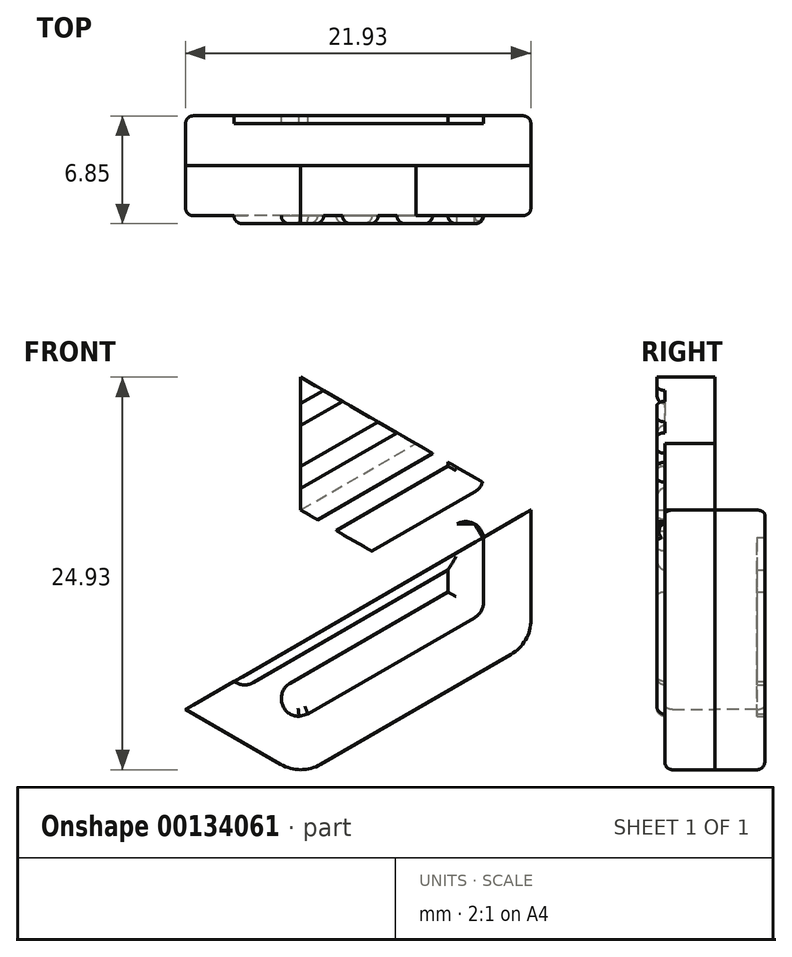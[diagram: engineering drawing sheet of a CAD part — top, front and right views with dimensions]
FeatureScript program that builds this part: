
annotation { "Feature Type Name" : "Feature", "Feature Type Description" : "" }
export const myFeature = defineFeature(function(context is Context, id is Id, definition is map)
    precondition{}
    {
        {
            var Q0;
            Q0=qCreatedBy(makeId("Front.planeOp"),FACE);
            var sketch = newSketch(context, id + "F0", { "sketchPlane" : qUnion([Q0])});
            skLineSegment(sketch, "E0", {"start": v(-0.1, -13.1) * mm, "end": v(-1.08, -12.54) * mm, "construction": true});
            skLineSegment(sketch, "E1", {"start": v(-1.08, -12.54) * mm, "end": v(-0.66, -11) * mm, "construction": true});
            skLineSegment(sketch, "E2", {"start": v(-0.66, -11) * mm, "end": v(9.36, -5.21) * mm});
            skLineSegment(sketch, "E3", {"start": v(9.36, -5.21) * mm, "end": v(9.36, -3.82) * mm});
            skLineSegment(sketch, "E4", {"start": v(9.36, -3.82) * mm, "end": v(-3, -10.95) * mm});
            skLineSegment(sketch, "E5", {"start": v(-3, -10.95) * mm, "end": v(-4.12, -10.95) * mm, "construction": true});
            skLineSegment(sketch, "E6", {"start": v(-4.12, -10.95) * mm, "end": v(-7.6, -8.96) * mm});
            skLineSegment(sketch, "E7", {"start": v(-7.6, -8.96) * mm, "end": v(-8.16, -7.98) * mm, "construction": true});
            skLineSegment(sketch, "E8", {"start": v(-8.16, -7.98) * mm, "end": v(-7.6, -7) * mm, "construction": true});
            skLineSegment(sketch, "E9", {"start": v(-7.6, -7) * mm, "end": v(9.36, 2.78) * mm});
            skLineSegment(sketch, "E10", {"start": v(9.36, 2.78) * mm, "end": v(9.36, 4.18) * mm});
            skLineSegment(sketch, "E11", {"start": v(9.36, 4.18) * mm, "end": v(-9.92, -6.96) * mm});
            skLineSegment(sketch, "E12", {"start": v(-9.92, -6.96) * mm, "end": v(-11.05, -6.96) * mm, "construction": true});
            skLineSegment(sketch, "E13", {"start": v(-11.05, -6.96) * mm, "end": v(-11.62, -5.98) * mm, "construction": true});
            skLineSegment(sketch, "E14", {"start": v(-11.62, -5.98) * mm, "end": v(-11.62, -1.98) * mm});
            skLineSegment(sketch, "E15", {"start": v(-11.62, -1.98) * mm, "end": v(-11.05, -1) * mm, "construction": true});
            skLineSegment(sketch, "E16", {"start": v(-11.05, -1) * mm, "end": v(4.78, 8.13) * mm});
            skLineSegment(sketch, "E17", {"start": v(4.78, 8.13) * mm, "end": v(3.57, 8.82) * mm});
            skLineSegment(sketch, "E18", {"start": v(3.57, 8.82) * mm, "end": v(-9.93, 1.04) * mm});
            skLineSegment(sketch, "E19", {"start": v(-9.93, 1.04) * mm, "end": v(-11.05, 1.04) * mm, "construction": true});
            skLineSegment(sketch, "E20", {"start": v(-11.05, 1.04) * mm, "end": v(-11.62, 2.02) * mm, "construction": true});
            skLineSegment(sketch, "E21", {"start": v(-11.62, 2.02) * mm, "end": v(-11.62, 6.01) * mm});
            skLineSegment(sketch, "E22", {"start": v(-11.62, 6.01) * mm, "end": v(-11.05, 7) * mm, "construction": true});
            skLineSegment(sketch, "E23", {"start": v(-11.05, 7) * mm, "end": v(-0.46, 13.1) * mm});
            skLineSegment(sketch, "E24", {"start": v(-0.46, 13.1) * mm, "end": v(1.08, 12.7) * mm, "construction": true});
            skLineSegment(sketch, "E25", {"start": v(1.08, 12.7) * mm, "end": v(0.67, 11.15) * mm, "construction": true});
            skLineSegment(sketch, "E26", {"start": v(0.67, 11.15) * mm, "end": v(-9.36, 5.36) * mm});
            skLineSegment(sketch, "E27", {"start": v(-9.36, 5.36) * mm, "end": v(-9.36, 3.97) * mm});
            skLineSegment(sketch, "E28", {"start": v(-9.36, 3.97) * mm, "end": v(3, 11.1) * mm});
            skLineSegment(sketch, "E29", {"start": v(3, 11.1) * mm, "end": v(4.14, 11.1) * mm, "construction": true});
            skLineSegment(sketch, "E30", {"start": v(4.14, 11.1) * mm, "end": v(7.6, 9.1) * mm});
            skLineSegment(sketch, "E31", {"start": v(7.6, 9.1) * mm, "end": v(8.16, 8.13) * mm, "construction": true});
            skLineSegment(sketch, "E32", {"start": v(8.16, 8.13) * mm, "end": v(7.6, 7.15) * mm, "construction": true});
            skLineSegment(sketch, "E33", {"start": v(7.6, 7.15) * mm, "end": v(-9.36, -2.63) * mm});
            skLineSegment(sketch, "E34", {"start": v(-9.36, -2.63) * mm, "end": v(-9.36, -4.03) * mm});
            skLineSegment(sketch, "E35", {"start": v(-9.36, -4.03) * mm, "end": v(9.93, 7.1) * mm});
            skLineSegment(sketch, "E36", {"start": v(9.93, 7.1) * mm, "end": v(11.05, 7.1) * mm, "construction": true});
            skLineSegment(sketch, "E37", {"start": v(11.05, 7.1) * mm, "end": v(11.62, 6.13) * mm, "construction": true});
            skLineSegment(sketch, "E38", {"start": v(11.62, 6.13) * mm, "end": v(11.62, 2.13) * mm});
            skLineSegment(sketch, "E39", {"start": v(11.62, 2.13) * mm, "end": v(11.05, 1.16) * mm, "construction": true});
            skLineSegment(sketch, "E40", {"start": v(11.05, 1.16) * mm, "end": v(-4.77, -7.98) * mm});
            skLineSegment(sketch, "E41", {"start": v(-4.77, -7.98) * mm, "end": v(-3.56, -8.67) * mm});
            skLineSegment(sketch, "E42", {"start": v(-3.56, -8.67) * mm, "end": v(9.93, -0.89) * mm});
            skLineSegment(sketch, "E43", {"start": v(9.93, -0.89) * mm, "end": v(11.05, -0.89) * mm, "construction": true});
            skLineSegment(sketch, "E44", {"start": v(11.05, -0.89) * mm, "end": v(11.62, -1.86) * mm, "construction": true});
            skLineSegment(sketch, "E45", {"start": v(11.62, -1.86) * mm, "end": v(11.62, -5.86) * mm});
            skLineSegment(sketch, "E46", {"start": v(11.62, -5.86) * mm, "end": v(11.05, -6.84) * mm, "construction": true});
            skLineSegment(sketch, "E47", {"start": v(11.05, -6.84) * mm, "end": v(0.46, -12.95) * mm});
            skLineSegment(sketch, "E48", {"start": v(0.46, -12.95) * mm, "end": v(-0.1, -13.1) * mm});
            skArc(sketch, "E49", {"start": v(0.67, 11.15) * mm, "mid": v(1.08, 12.7) * mm, "end": v(-0.46, 13.1) * mm});
            skArc(sketch, "E50", {"start": v(-11.05, 7) * mm, "mid": v(-11.47, 6.58) * mm, "end": v(-11.62, 6.01) * mm});
            skArc(sketch, "E51", {"start": v(-11.62, 2.02) * mm, "mid": v(-11.05, 1.04) * mm, "end": v(-9.93, 1.04) * mm});
            skArc(sketch, "E52", {"start": v(4.14, 11.1) * mm, "mid": v(3.57, 11.25) * mm, "end": v(3, 11.1) * mm});
            skArc(sketch, "E53", {"start": v(7.6, 7.15) * mm, "mid": v(8.16, 8.13) * mm, "end": v(7.6, 9.1) * mm});
            skArc(sketch, "E54", {"start": v(-11.05, -1) * mm, "mid": v(-11.47, -1.42) * mm, "end": v(-11.62, -1.98) * mm});
            skArc(sketch, "E55", {"start": v(-11.62, -5.98) * mm, "mid": v(-11.05, -6.96) * mm, "end": v(-9.92, -6.96) * mm});
            skArc(sketch, "E56", {"start": v(11.62, 6.13) * mm, "mid": v(11.05, 7.1) * mm, "end": v(9.93, 7.1) * mm});
            skArc(sketch, "E57", {"start": v(11.05, 1.16) * mm, "mid": v(11.47, 1.57) * mm, "end": v(11.62, 2.13) * mm});
            skArc(sketch, "E58", {"start": v(-7.6, -7) * mm, "mid": v(-8.16, -7.98) * mm, "end": v(-7.6, -8.96) * mm});
            skArc(sketch, "E59", {"start": v(-4.12, -10.95) * mm, "mid": v(-3.56, -11.1) * mm, "end": v(-3, -10.95) * mm});
            skArc(sketch, "E60", {"start": v(11.62, -1.86) * mm, "mid": v(11.05, -0.89) * mm, "end": v(9.93, -0.89) * mm});
            skArc(sketch, "E61", {"start": v(11.05, -6.84) * mm, "mid": v(11.47, -6.43) * mm, "end": v(11.62, -5.86) * mm});
            skArc(sketch, "E62", {"start": v(-0.66, -11) * mm, "mid": v(-1.2, -12.27) * mm, "end": v(-0.1, -13.1) * mm});
            skSolve(sketch);
        }
        {
            var Q0;
            Q0=qCreatedBy(makeId("Front.planeOp"),FACE);
            var sketch = newSketch(context, id + "F1", { "sketchPlane" : qUnion([Q0])});
            skLineSegment(sketch, "E63", {"start": v(1.27, -16.15) * mm, "end": v(13.35, -9.18) * mm});
            skLineSegment(sketch, "E64", {"start": v(14.62, -6.98) * mm, "end": v(14.62, 0) * mm});
            skLineSegment(sketch, "E65", {"start": v(14.62, 0) * mm, "end": v(0, 8.44) * mm});
            skLineSegment(sketch, "E66", {"start": v(0, 8.44) * mm, "end": v(0, 0) * mm});
            skLineSegment(sketch, "E67", {"start": v(0, 0) * mm, "end": v(-7.31, 4.22) * mm});
            skLineSegment(sketch, "E68", {"start": v(-7.31, 4.22) * mm, "end": v(-7.31, -12.66) * mm});
            skLineSegment(sketch, "E69", {"start": v(-1.27, -16.15) * mm, "end": v(-7.31, -12.66) * mm});
            skLineSegment(sketch, "E70", {"start": v(0, 0) * mm, "end": v(0, -8.44) * mm});
            skLineSegment(sketch, "E71", {"start": v(0, -8.44) * mm, "end": v(7.31, -4.22) * mm});
            skLineSegment(sketch, "E72", {"start": v(7.31, -4.22) * mm, "end": v(0, 0) * mm});
            skLineSegment(sketch, "E73", {"start": v(-7.31, -12.66) * mm, "end": v(14.62, 0) * mm});
            skLineSegment(sketch, "E74", {"start": v(0, 0) * mm, "end": v(3.66, -6.33) * mm, "construction": true});
            skLineSegment(sketch, "E75", {"start": v(7.31, -12.67) * mm, "end": v(3.66, -6.33) * mm, "construction": true});
            skPoint(sketch, "E76.visualSharp", {"position": v(0, -16.89) * mm});
            skArc(sketch, "E76.filletArc", {"start": v(-1.27, -16.15) * mm, "mid": v(0, -16.5) * mm, "end": v(1.27, -16.15) * mm});
            skPoint(sketch, "E77.visualSharp", {"position": v(14.62, -8.44) * mm});
            skArc(sketch, "E77.filletArc", {"start": v(13.35, -9.18) * mm, "mid": v(14.28, -8.25) * mm, "end": v(14.62, -6.98) * mm});
            skPoint(sketch, "E78.1.0", {"position": v(0, 16.89) * mm});
            skLineSegment(sketch, "E78.1.1", {"start": v(0, -8.44) * mm, "end": v(14.62, 0) * mm});
            skLineSegment(sketch, "E78.1.2", {"start": v(14.62, 0) * mm, "end": v(-7.31, 12.67) * mm});
            skLineSegment(sketch, "E78.1.3", {"start": v(13.35, 9.18) * mm, "end": v(1.27, 16.15) * mm});
            skLineSegment(sketch, "E78.1.5", {"start": v(-7.31, -4.22) * mm, "end": v(0, 0) * mm});
            skLineSegment(sketch, "E78.1.6", {"start": v(-7.31, 12.67) * mm, "end": v(-7.31, -4.22) * mm});
            skLineSegment(sketch, "E78.1.7", {"start": v(14.62, 6.98) * mm, "end": v(14.62, 0) * mm});
            skLineSegment(sketch, "E78.1.8", {"start": v(0, 0) * mm, "end": v(7.31, 4.22) * mm});
            skLineSegment(sketch, "E78.1.10", {"start": v(0, 0) * mm, "end": v(3.66, 6.33) * mm, "construction": true});
            skLineSegment(sketch, "E78.1.11", {"start": v(7.31, 12.66) * mm, "end": v(3.66, 6.33) * mm, "construction": true});
            skLineSegment(sketch, "E78.1.12", {"start": v(-1.27, 16.15) * mm, "end": v(-7.31, 12.67) * mm});
            skPoint(sketch, "E78.1.13", {"position": v(14.62, 8.44) * mm});
            skArc(sketch, "E78.1.14", {"start": v(14.62, 6.98) * mm, "mid": v(14.28, 8.25) * mm, "end": v(13.35, 9.18) * mm});
            skLineSegment(sketch, "E78.1.15", {"start": v(7.31, 4.22) * mm, "end": v(0, 8.44) * mm});
            skArc(sketch, "E78.1.16", {"start": v(1.27, 16.15) * mm, "mid": v(0, 16.5) * mm, "end": v(-1.27, 16.15) * mm});
            skPoint(sketch, "E78.2.0", {"position": v(-14.62, -8.44) * mm});
            skLineSegment(sketch, "E78.2.1", {"start": v(7.31, 4.22) * mm, "end": v(-7.31, 12.67) * mm});
            skLineSegment(sketch, "E78.2.2", {"start": v(-7.31, 12.67) * mm, "end": v(-7.31, -12.66) * mm});
            skLineSegment(sketch, "E78.2.3", {"start": v(-14.62, 6.98) * mm, "end": v(-14.62, -6.98) * mm});
            skLineSegment(sketch, "E78.2.4", {"start": v(0, 0) * mm, "end": v(7.31, 4.22) * mm});
            skLineSegment(sketch, "E78.2.6", {"start": v(-7.31, -12.66) * mm, "end": v(7.31, -4.22) * mm});
            skLineSegment(sketch, "E78.2.7", {"start": v(-13.35, 9.18) * mm, "end": v(-7.31, 12.67) * mm});
            skLineSegment(sketch, "E78.2.9", {"start": v(-7.31, -4.22) * mm, "end": v(0, 0) * mm});
            skLineSegment(sketch, "E78.2.10", {"start": v(0, 0) * mm, "end": v(-7.31, 0) * mm, "construction": true});
            skLineSegment(sketch, "E78.2.11", {"start": v(-14.62, 0) * mm, "end": v(-7.31, 0) * mm, "construction": true});
            skLineSegment(sketch, "E78.2.12", {"start": v(-13.35, -9.18) * mm, "end": v(-7.31, -12.66) * mm});
            skPoint(sketch, "E78.2.13", {"position": v(-14.62, 8.44) * mm});
            skArc(sketch, "E78.2.14", {"start": v(-13.35, 9.18) * mm, "mid": v(-14.28, 8.25) * mm, "end": v(-14.62, 6.98) * mm});
            skLineSegment(sketch, "E78.2.15", {"start": v(-7.31, 4.22) * mm, "end": v(-7.31, -4.22) * mm});
            skArc(sketch, "E78.2.16", {"start": v(-14.62, -6.98) * mm, "mid": v(-14.28, -8.25) * mm, "end": v(-13.35, -9.18) * mm});
            skPoint(sketch, "E78.center", {"position": v(0, 0) * mm});
            skSolve(sketch);
        }
        {
            var Q0;
            Q0=makeQuery(id+"F1.imprint","IMPRINT",FACE,{"disambiguationData":[TD([[makeQuery(id+"F1.imprint","IMPRINT",EDGE,{"derivedFrom":sQuery(id+"F1.wireOp",EDGE,"E63")}),1.0]])]});
            var Q1;
            {var subQ0=sQuery(id+"F1.wireOp",EDGE,"E65");Q1=makeQuery(id+"F1.imprint","IMPRINT",FACE,{"disambiguationData":[TD([[makeQuery(id+"F1.imprint","IMPRINT",EDGE,{"derivedFrom":subQ0}),1.0]])]});}
            var Q2;
            Q2=makeQuery(id+"F1.imprint","IMPRINT",FACE,{"disambiguationData":[TD([[makeQuery(id+"F1.imprint","IMPRINT",EDGE,{"derivedFrom":sQuery(id+"F1.wireOp",EDGE,"E78.1.1")}),1.0]])]});
            var Q3;
            {var subQ0=sQuery(id+"F1.wireOp",EDGE,"E66");Q3=makeQuery(id+"F1.imprint","IMPRINT",FACE,{"disambiguationData":[TD([[makeQuery(id+"F1.imprint","IMPRINT",EDGE,{"derivedFrom":subQ0}),1.0]])]});}
            extrude(context, id + "F2", {"entities" : qUnion([Q0, Q1, Q2, Q3]), "depth" : 3.17 * mm});
        }
        {
            var Q0;
            Q0=makeQuery(id+"F1.imprint","IMPRINT",FACE,{"disambiguationData":[TD([[makeQuery(id+"F1.imprint","IMPRINT",EDGE,{"derivedFrom":sQuery(id+"F1.wireOp",EDGE,"E63")}),1.0]])]});
            var Q1;
            Q1=makeQuery(id+"F1.imprint","IMPRINT",FACE,{"disambiguationData":[TD([[makeQuery(id+"F1.imprint","IMPRINT",EDGE,{"derivedFrom":sQuery(id+"F1.wireOp",EDGE,"E67")}),1.0]])]});
            var Q2;
            {var subQ0=sQuery(id+"F1.wireOp",EDGE,"E70");Q2=makeQuery(id+"F1.imprint","IMPRINT",FACE,{"disambiguationData":[TD([[makeQuery(id+"F1.imprint","IMPRINT",EDGE,{"derivedFrom":subQ0}),-1.0]])]});}
            extrude(context, id + "F3", {"entities" : qUnion([Q0, Q1, Q2]), "oppositeDirection" : true, "depth" : 3.17 * mm});
        }
        {
            var Q0;
            Q0=makeQuery(id+"F2.opExtrude","CAP_FACE",FACE,{"disambiguationData":[OSD([sQuery(id+"F1.wireOp",EDGE,"E63"),sQuery(id+"F1.wireOp",EDGE,"E64"),sQuery(id+"F1.wireOp",EDGE,"E69"),sQuery(id+"F1.wireOp",EDGE,"E76.filletArc"),sQuery(id+"F1.wireOp",EDGE,"E77.filletArc"),sQuery(id+"F1.wireOp",EDGE,"E78.1.2"),sQuery(id+"F1.wireOp",EDGE,"E66"),sQuery(id+"F1.wireOp",EDGE,"E78.2.1"),sQuery(id+"F1.wireOp",EDGE,"E72"),sQuery(id+"F1.wireOp",EDGE,"E78.2.6")])],"isStart":false});
            var sketch = newSketch(context, id + "F4", { "sketchPlane" : qUnion([Q0])});
            skLineSegment(sketch, "E79.0", {"start": v(-0.1, -13.1) * mm, "end": v(-1.08, -12.54) * mm});
            skLineSegment(sketch, "E79.1", {"start": v(-1.08, -12.54) * mm, "end": v(-0.66, -11) * mm});
            skLineSegment(sketch, "E79.2", {"start": v(-0.66, -11) * mm, "end": v(9.36, -5.21) * mm});
            skLineSegment(sketch, "E79.3", {"start": v(9.36, -5.21) * mm, "end": v(9.36, -3.82) * mm});
            skLineSegment(sketch, "E79.4", {"start": v(9.36, -3.82) * mm, "end": v(-3, -10.95) * mm});
            skLineSegment(sketch, "E79.5", {"start": v(-3, -10.95) * mm, "end": v(-4.12, -10.95) * mm});
            skLineSegment(sketch, "E79.6", {"start": v(-4.12, -10.95) * mm, "end": v(-7.6, -8.96) * mm});
            skLineSegment(sketch, "E79.7", {"start": v(-7.6, -8.96) * mm, "end": v(-8.16, -7.98) * mm});
            skLineSegment(sketch, "E79.8", {"start": v(-8.16, -7.98) * mm, "end": v(-7.6, -7) * mm});
            skLineSegment(sketch, "E79.9", {"start": v(-7.6, -7) * mm, "end": v(9.36, 2.78) * mm});
            skLineSegment(sketch, "E79.10", {"start": v(9.36, 2.78) * mm, "end": v(9.36, 4.18) * mm});
            skLineSegment(sketch, "E79.11", {"start": v(9.36, 4.18) * mm, "end": v(-9.92, -6.96) * mm});
            skLineSegment(sketch, "E79.12", {"start": v(-9.92, -6.96) * mm, "end": v(-11.05, -6.96) * mm});
            skLineSegment(sketch, "E79.13", {"start": v(-11.05, -6.96) * mm, "end": v(-11.62, -5.98) * mm});
            skLineSegment(sketch, "E79.14", {"start": v(-11.62, -5.98) * mm, "end": v(-11.62, -1.98) * mm});
            skLineSegment(sketch, "E79.15", {"start": v(-11.62, -1.98) * mm, "end": v(-11.05, -1) * mm});
            skLineSegment(sketch, "E79.16", {"start": v(-11.05, -1) * mm, "end": v(4.78, 8.13) * mm});
            skLineSegment(sketch, "E79.17", {"start": v(4.78, 8.13) * mm, "end": v(3.57, 8.82) * mm});
            skLineSegment(sketch, "E79.18", {"start": v(3.57, 8.82) * mm, "end": v(-9.93, 1.04) * mm});
            skLineSegment(sketch, "E79.19", {"start": v(-9.93, 1.04) * mm, "end": v(-11.05, 1.04) * mm});
            skLineSegment(sketch, "E79.20", {"start": v(-11.05, 1.04) * mm, "end": v(-11.62, 2.02) * mm});
            skLineSegment(sketch, "E79.21", {"start": v(-11.62, 2.02) * mm, "end": v(-11.62, 6.01) * mm});
            skLineSegment(sketch, "E79.22", {"start": v(-11.62, 6.01) * mm, "end": v(-11.05, 7) * mm});
            skLineSegment(sketch, "E79.23", {"start": v(-11.05, 7) * mm, "end": v(-0.46, 13.1) * mm});
            skLineSegment(sketch, "E79.24", {"start": v(-0.46, 13.1) * mm, "end": v(1.08, 12.7) * mm});
            skLineSegment(sketch, "E79.25", {"start": v(1.08, 12.7) * mm, "end": v(0.67, 11.15) * mm});
            skLineSegment(sketch, "E79.26", {"start": v(0.67, 11.15) * mm, "end": v(-9.36, 5.36) * mm});
            skLineSegment(sketch, "E79.27", {"start": v(-9.36, 5.36) * mm, "end": v(-9.36, 3.97) * mm});
            skLineSegment(sketch, "E79.28", {"start": v(-9.36, 3.97) * mm, "end": v(3, 11.1) * mm});
            skLineSegment(sketch, "E79.29", {"start": v(3, 11.1) * mm, "end": v(4.14, 11.1) * mm});
            skLineSegment(sketch, "E79.30", {"start": v(4.14, 11.1) * mm, "end": v(7.6, 9.1) * mm});
            skLineSegment(sketch, "E79.31", {"start": v(7.6, 9.1) * mm, "end": v(8.16, 8.13) * mm});
            skLineSegment(sketch, "E79.32", {"start": v(8.16, 8.13) * mm, "end": v(7.6, 7.15) * mm});
            skLineSegment(sketch, "E79.33", {"start": v(7.6, 7.15) * mm, "end": v(-9.36, -2.63) * mm});
            skLineSegment(sketch, "E79.34", {"start": v(-9.36, -2.63) * mm, "end": v(-9.36, -4.03) * mm});
            skLineSegment(sketch, "E79.35", {"start": v(-9.36, -4.03) * mm, "end": v(9.93, 7.1) * mm});
            skLineSegment(sketch, "E79.36", {"start": v(9.93, 7.1) * mm, "end": v(11.05, 7.1) * mm});
            skLineSegment(sketch, "E79.37", {"start": v(11.05, 7.1) * mm, "end": v(11.62, 6.13) * mm});
            skLineSegment(sketch, "E79.38", {"start": v(11.62, 6.13) * mm, "end": v(11.62, 2.13) * mm});
            skLineSegment(sketch, "E79.39", {"start": v(11.62, 2.13) * mm, "end": v(11.05, 1.16) * mm});
            skLineSegment(sketch, "E79.40", {"start": v(11.05, 1.16) * mm, "end": v(-4.77, -7.98) * mm});
            skLineSegment(sketch, "E79.41", {"start": v(-4.77, -7.98) * mm, "end": v(-3.56, -8.67) * mm});
            skLineSegment(sketch, "E79.42", {"start": v(-3.56, -8.67) * mm, "end": v(9.93, -0.89) * mm});
            skLineSegment(sketch, "E79.43", {"start": v(9.93, -0.89) * mm, "end": v(11.05, -0.89) * mm});
            skLineSegment(sketch, "E79.44", {"start": v(11.05, -0.89) * mm, "end": v(11.62, -1.86) * mm});
            skLineSegment(sketch, "E79.45", {"start": v(11.62, -1.86) * mm, "end": v(11.62, -5.86) * mm});
            skLineSegment(sketch, "E79.46", {"start": v(11.62, -5.86) * mm, "end": v(11.05, -6.84) * mm});
            skLineSegment(sketch, "E79.47", {"start": v(11.05, -6.84) * mm, "end": v(0.46, -12.95) * mm});
            skLineSegment(sketch, "E79.48", {"start": v(0.46, -12.95) * mm, "end": v(-0.1, -13.1) * mm});
            skArc(sketch, "E79.49", {"start": v(0.67, 11.15) * mm, "mid": v(1.08, 12.7) * mm, "end": v(-0.46, 13.1) * mm});
            skArc(sketch, "E79.50", {"start": v(-11.05, 7) * mm, "mid": v(-11.47, 6.58) * mm, "end": v(-11.62, 6.01) * mm});
            skArc(sketch, "E79.51", {"start": v(-11.62, 2.02) * mm, "mid": v(-11.05, 1.04) * mm, "end": v(-9.93, 1.04) * mm});
            skArc(sketch, "E79.52", {"start": v(4.14, 11.1) * mm, "mid": v(3.57, 11.25) * mm, "end": v(3, 11.1) * mm});
            skArc(sketch, "E79.53", {"start": v(7.6, 7.15) * mm, "mid": v(8.16, 8.13) * mm, "end": v(7.6, 9.1) * mm});
            skArc(sketch, "E79.54", {"start": v(-11.05, -1) * mm, "mid": v(-11.47, -1.42) * mm, "end": v(-11.62, -1.98) * mm});
            skArc(sketch, "E79.55", {"start": v(-11.62, -5.98) * mm, "mid": v(-11.05, -6.96) * mm, "end": v(-9.92, -6.96) * mm});
            skArc(sketch, "E79.56", {"start": v(11.62, 6.13) * mm, "mid": v(11.05, 7.1) * mm, "end": v(9.93, 7.1) * mm});
            skArc(sketch, "E79.57", {"start": v(11.05, 1.16) * mm, "mid": v(11.47, 1.57) * mm, "end": v(11.62, 2.13) * mm});
            skArc(sketch, "E79.58", {"start": v(-7.6, -7) * mm, "mid": v(-8.16, -7.98) * mm, "end": v(-7.6, -8.96) * mm});
            skArc(sketch, "E79.59", {"start": v(-4.12, -10.95) * mm, "mid": v(-3.56, -11.1) * mm, "end": v(-3, -10.95) * mm});
            skArc(sketch, "E79.60", {"start": v(11.62, -1.86) * mm, "mid": v(11.05, -0.89) * mm, "end": v(9.93, -0.89) * mm});
            skArc(sketch, "E79.61", {"start": v(11.05, -6.84) * mm, "mid": v(11.47, -6.43) * mm, "end": v(11.62, -5.86) * mm});
            skArc(sketch, "E79.62", {"start": v(-0.66, -11) * mm, "mid": v(-1.2, -12.27) * mm, "end": v(-0.1, -13.1) * mm});
            skLineSegment(sketch, "E80.0", {"start": v(-1.27, -16.15) * mm, "end": v(-7.31, -12.66) * mm});
            skArc(sketch, "E80.1", {"start": v(-1.27, -16.15) * mm, "mid": v(0, -16.5) * mm, "end": v(1.27, -16.15) * mm});
            skLineSegment(sketch, "E80.2", {"start": v(1.27, -16.15) * mm, "end": v(13.35, -9.18) * mm});
            skArc(sketch, "E80.3", {"start": v(13.35, -9.18) * mm, "mid": v(14.28, -8.25) * mm, "end": v(14.62, -6.98) * mm});
            skLineSegment(sketch, "E80.4", {"start": v(14.62, -6.98) * mm, "end": v(14.62, 0) * mm});
            skLineSegment(sketch, "E80.5", {"start": v(-7.31, -12.66) * mm, "end": v(7.31, -4.22) * mm});
            skLineSegment(sketch, "E80.6", {"start": v(14.62, 0) * mm, "end": v(0, 8.44) * mm});
            skLineSegment(sketch, "E80.7", {"start": v(7.31, -4.22) * mm, "end": v(0, 0) * mm});
            skLineSegment(sketch, "E80.8", {"start": v(0, 8.44) * mm, "end": v(0, 0) * mm});
            skSolve(sketch);
        }
        {
            var Q0;
            Q0=makeQuery(id+"F3.opExtrude","CAP_FACE",FACE,{"disambiguationData":[OSD([sQuery(id+"F1.wireOp",EDGE,"E63"),sQuery(id+"F1.wireOp",EDGE,"E64"),sQuery(id+"F1.wireOp",EDGE,"E69"),sQuery(id+"F1.wireOp",EDGE,"E76.filletArc"),sQuery(id+"F1.wireOp",EDGE,"E77.filletArc"),sQuery(id+"F1.wireOp",EDGE,"E78.1.1"),sQuery(id+"F1.wireOp",EDGE,"E70"),sQuery(id+"F1.wireOp",EDGE,"E78.2.2"),sQuery(id+"F1.wireOp",EDGE,"E78.2.6"),sQuery(id+"F1.wireOp",EDGE,"E67"),sQuery(id+"F1.wireOp",EDGE,"E78.2.15")])],"isStart":false});
            var sketch = newSketch(context, id + "F5", { "sketchPlane" : qUnion([Q0])});
            skLineSegment(sketch, "E81.0", {"start": v(0.1, -13.1) * mm, "end": v(1.08, -12.54) * mm});
            skLineSegment(sketch, "E81.1", {"start": v(1.08, -12.54) * mm, "end": v(0.66, -11) * mm});
            skLineSegment(sketch, "E81.2", {"start": v(0.66, -11) * mm, "end": v(-9.36, -5.21) * mm});
            skLineSegment(sketch, "E81.3", {"start": v(-9.36, -5.21) * mm, "end": v(-9.36, -3.82) * mm});
            skLineSegment(sketch, "E81.4", {"start": v(-9.36, -3.82) * mm, "end": v(3, -10.95) * mm});
            skLineSegment(sketch, "E81.5", {"start": v(3, -10.95) * mm, "end": v(4.12, -10.95) * mm});
            skLineSegment(sketch, "E81.6", {"start": v(4.12, -10.95) * mm, "end": v(7.6, -8.96) * mm});
            skLineSegment(sketch, "E81.7", {"start": v(7.6, -8.96) * mm, "end": v(8.16, -7.98) * mm});
            skLineSegment(sketch, "E81.8", {"start": v(8.16, -7.98) * mm, "end": v(7.6, -7) * mm});
            skLineSegment(sketch, "E81.9", {"start": v(7.6, -7) * mm, "end": v(-9.36, 2.78) * mm});
            skLineSegment(sketch, "E81.10", {"start": v(-9.36, 2.78) * mm, "end": v(-9.36, 4.18) * mm});
            skLineSegment(sketch, "E81.11", {"start": v(-9.36, 4.18) * mm, "end": v(9.92, -6.96) * mm});
            skLineSegment(sketch, "E81.12", {"start": v(9.92, -6.96) * mm, "end": v(11.05, -6.96) * mm});
            skLineSegment(sketch, "E81.13", {"start": v(11.05, -6.96) * mm, "end": v(11.62, -5.98) * mm});
            skLineSegment(sketch, "E81.14", {"start": v(11.62, -5.98) * mm, "end": v(11.62, -1.98) * mm});
            skLineSegment(sketch, "E81.15", {"start": v(11.62, -1.98) * mm, "end": v(11.05, -1) * mm});
            skLineSegment(sketch, "E81.16", {"start": v(11.05, -1) * mm, "end": v(-4.78, 8.13) * mm});
            skLineSegment(sketch, "E81.17", {"start": v(-4.78, 8.13) * mm, "end": v(-3.57, 8.82) * mm});
            skLineSegment(sketch, "E81.18", {"start": v(-3.57, 8.82) * mm, "end": v(9.93, 1.04) * mm});
            skLineSegment(sketch, "E81.19", {"start": v(9.93, 1.04) * mm, "end": v(11.05, 1.04) * mm});
            skLineSegment(sketch, "E81.20", {"start": v(11.05, 1.04) * mm, "end": v(11.62, 2.02) * mm});
            skLineSegment(sketch, "E81.21", {"start": v(11.62, 2.02) * mm, "end": v(11.62, 6.01) * mm});
            skLineSegment(sketch, "E81.22", {"start": v(11.62, 6.01) * mm, "end": v(11.05, 7) * mm});
            skLineSegment(sketch, "E81.23", {"start": v(11.05, 7) * mm, "end": v(0.46, 13.1) * mm});
            skLineSegment(sketch, "E81.24", {"start": v(0.46, 13.1) * mm, "end": v(-1.08, 12.7) * mm});
            skLineSegment(sketch, "E81.25", {"start": v(-1.08, 12.7) * mm, "end": v(-0.67, 11.15) * mm});
            skLineSegment(sketch, "E81.26", {"start": v(-0.67, 11.15) * mm, "end": v(9.36, 5.36) * mm});
            skLineSegment(sketch, "E81.27", {"start": v(9.36, 5.36) * mm, "end": v(9.36, 3.97) * mm});
            skLineSegment(sketch, "E81.28", {"start": v(9.36, 3.97) * mm, "end": v(-3, 11.1) * mm});
            skLineSegment(sketch, "E81.29", {"start": v(-3, 11.1) * mm, "end": v(-4.14, 11.1) * mm});
            skLineSegment(sketch, "E81.30", {"start": v(-4.14, 11.1) * mm, "end": v(-7.6, 9.1) * mm});
            skLineSegment(sketch, "E81.31", {"start": v(-7.6, 9.1) * mm, "end": v(-8.16, 8.13) * mm});
            skLineSegment(sketch, "E81.32", {"start": v(-8.16, 8.13) * mm, "end": v(-7.6, 7.15) * mm});
            skLineSegment(sketch, "E81.33", {"start": v(-7.6, 7.15) * mm, "end": v(9.36, -2.63) * mm});
            skLineSegment(sketch, "E81.34", {"start": v(9.36, -2.63) * mm, "end": v(9.36, -4.03) * mm});
            skLineSegment(sketch, "E81.35", {"start": v(9.36, -4.03) * mm, "end": v(-9.93, 7.1) * mm});
            skLineSegment(sketch, "E81.36", {"start": v(-9.93, 7.1) * mm, "end": v(-11.05, 7.1) * mm});
            skLineSegment(sketch, "E81.37", {"start": v(-11.05, 7.1) * mm, "end": v(-11.62, 6.13) * mm});
            skLineSegment(sketch, "E81.38", {"start": v(-11.62, 6.13) * mm, "end": v(-11.62, 2.13) * mm});
            skLineSegment(sketch, "E81.39", {"start": v(-11.62, 2.13) * mm, "end": v(-11.05, 1.16) * mm});
            skLineSegment(sketch, "E81.40", {"start": v(-11.05, 1.16) * mm, "end": v(4.77, -7.98) * mm});
            skLineSegment(sketch, "E81.41", {"start": v(4.77, -7.98) * mm, "end": v(3.56, -8.67) * mm});
            skLineSegment(sketch, "E81.42", {"start": v(3.56, -8.67) * mm, "end": v(-9.93, -0.89) * mm});
            skLineSegment(sketch, "E81.43", {"start": v(-9.93, -0.89) * mm, "end": v(-11.05, -0.89) * mm});
            skLineSegment(sketch, "E81.44", {"start": v(-11.05, -0.89) * mm, "end": v(-11.62, -1.86) * mm});
            skLineSegment(sketch, "E81.45", {"start": v(-11.62, -1.86) * mm, "end": v(-11.62, -5.86) * mm});
            skLineSegment(sketch, "E81.46", {"start": v(-11.62, -5.86) * mm, "end": v(-11.05, -6.84) * mm});
            skLineSegment(sketch, "E81.47", {"start": v(-11.05, -6.84) * mm, "end": v(-0.46, -12.95) * mm});
            skLineSegment(sketch, "E81.48", {"start": v(-0.46, -12.95) * mm, "end": v(0.1, -13.1) * mm});
            skArc(sketch, "E81.49", {"start": v(-0.67, 11.15) * mm, "mid": v(-1.08, 12.7) * mm, "end": v(0.46, 13.1) * mm});
            skArc(sketch, "E81.50", {"start": v(11.05, 7) * mm, "mid": v(11.47, 6.58) * mm, "end": v(11.62, 6.01) * mm});
            skArc(sketch, "E81.51", {"start": v(11.62, 2.02) * mm, "mid": v(11.05, 1.04) * mm, "end": v(9.93, 1.04) * mm});
            skArc(sketch, "E81.52", {"start": v(-4.14, 11.1) * mm, "mid": v(-3.57, 11.25) * mm, "end": v(-3, 11.1) * mm});
            skArc(sketch, "E81.53", {"start": v(-7.6, 7.15) * mm, "mid": v(-8.16, 8.13) * mm, "end": v(-7.6, 9.1) * mm});
            skArc(sketch, "E81.54", {"start": v(11.05, -1) * mm, "mid": v(11.47, -1.42) * mm, "end": v(11.62, -1.98) * mm});
            skArc(sketch, "E81.55", {"start": v(11.62, -5.98) * mm, "mid": v(11.05, -6.96) * mm, "end": v(9.92, -6.96) * mm});
            skArc(sketch, "E81.56", {"start": v(-11.62, 6.13) * mm, "mid": v(-11.05, 7.1) * mm, "end": v(-9.93, 7.1) * mm});
            skArc(sketch, "E81.57", {"start": v(-11.05, 1.16) * mm, "mid": v(-11.47, 1.57) * mm, "end": v(-11.62, 2.13) * mm});
            skArc(sketch, "E81.58", {"start": v(7.6, -7) * mm, "mid": v(8.16, -7.98) * mm, "end": v(7.6, -8.96) * mm});
            skArc(sketch, "E81.59", {"start": v(4.12, -10.95) * mm, "mid": v(3.56, -11.1) * mm, "end": v(3, -10.95) * mm});
            skArc(sketch, "E81.60", {"start": v(-11.62, -1.86) * mm, "mid": v(-11.05, -0.89) * mm, "end": v(-9.93, -0.89) * mm});
            skArc(sketch, "E81.61", {"start": v(-11.05, -6.84) * mm, "mid": v(-11.47, -6.43) * mm, "end": v(-11.62, -5.86) * mm});
            skArc(sketch, "E81.62", {"start": v(0.66, -11) * mm, "mid": v(1.2, -12.27) * mm, "end": v(0.1, -13.1) * mm});
            skSolve(sketch);
        }
        {
            var Q0;
            Q0 = qSketchRegion(id + "F5", true);
            extrude(context, id + "F6", {"entities" : qUnion([Q0]), "operationType" : NewBodyOperationType.REMOVE, "oppositeDirection" : true, "depth" : .5 * mm});
        }
        {
            var Q0;
            Q0=makeQuery(id+"F4.imprint","IMPRINT",FACE,{"disambiguationData":[TD([[makeQuery(id+"F4.imprint","IMPRINT",EDGE,{"derivedFrom":sQuery(id+"F4.wireOp",EDGE,"E79.46")}),1.0]])]});
            var Q1;
            {var subQ0=sQuery(id+"F4.wireOp",EDGE,"E79.44");Q1=makeQuery(id+"F4.imprint","IMPRINT",FACE,{"disambiguationData":[TD([[makeQuery(id+"F4.imprint","IMPRINT",EDGE,{"derivedFrom":subQ0}),1.0]])]});}
            var Q2;
            {var subQ0=sQuery(id+"F4.wireOp",EDGE,"E79.43");Q2=makeQuery(id+"F4.imprint","IMPRINT",FACE,{"disambiguationData":[TD([[makeQuery(id+"F4.imprint","IMPRINT",EDGE,{"derivedFrom":subQ0}),1.0]])]});}
            var Q3;
            Q3=makeQuery(id+"F4.imprint","IMPRINT",FACE,{"disambiguationData":[TD([[makeQuery(id+"F4.imprint","IMPRINT",EDGE,{"derivedFrom":sQuery(id+"F4.wireOp",EDGE,"E79.5")}),1.0]])]});
            var Q4;
            {var subQ0=sQuery(id+"F4.wireOp",EDGE,"E79.1");Q4=makeQuery(id+"F4.imprint","IMPRINT",FACE,{"disambiguationData":[TD([[makeQuery(id+"F4.imprint","IMPRINT",EDGE,{"derivedFrom":subQ0}),1.0]])]});}
            var Q5;
            {var subQ0=sQuery(id+"F4.wireOp",EDGE,"E79.0");Q5=makeQuery(id+"F4.imprint","IMPRINT",FACE,{"disambiguationData":[TD([[makeQuery(id+"F4.imprint","IMPRINT",EDGE,{"derivedFrom":subQ0}),1.0]])]});}
            var Q6;
            {var subQ0=sQuery(id+"F4.wireOp",EDGE,"E79.57");var subQ3=sQuery(id+"F4.wireOp",EDGE,"E80.6");var subQ5=makeQuery(id+"F4.imprint","INTERSECT",VERTEX,{"derivedFrom":[subQ0,subQ3]});Q6=makeQuery(id+"F4.imprint","IMPRINT",FACE,{"disambiguationData":[TD([[makeQuery(id+"F4.imprint","IMPRINT",EDGE,{"disambiguationData":[TD([[subQ5,-1.0]])],"derivedFrom":subQ3}),1.0]])]});}
            var Q7;
            Q7=makeQuery(id+"F4.imprint","IMPRINT",FACE,{"disambiguationData":[TD([[makeQuery(id+"F4.imprint","IMPRINT",EDGE,{"derivedFrom":sQuery(id+"F4.wireOp",EDGE,"E79.0")}),-1.0]])]});
            var Q8;
            {var subQ7=sQuery(id+"F4.wireOp",EDGE,"E79.10");var subQ8=sQuery(id+"F4.wireOp",EDGE,"E79.9");var subQ9=makeQuery(id+"F4.imprint","INTERSECT",VERTEX,{"derivedFrom":[subQ8,subQ7]});Q8=makeQuery(id+"F4.imprint","IMPRINT",FACE,{"disambiguationData":[TD([[makeQuery(id+"F4.imprint","IMPRINT",EDGE,{"disambiguationData":[TD([[subQ9,1.0]])],"derivedFrom":subQ8}),-1.0]])]});}
            var Q9;
            {var subQ1=sQuery(id+"F4.wireOp",EDGE,"E80.7");var subQ3=sQuery(id+"F4.wireOp",EDGE,"E79.11");var subQ4=makeQuery(id+"F4.imprint","INTERSECT",VERTEX,{"derivedFrom":[subQ3,subQ1]});Q9=makeQuery(id+"F4.imprint","IMPRINT",FACE,{"disambiguationData":[TD([[makeQuery(id+"F4.imprint","IMPRINT",EDGE,{"disambiguationData":[TD([[subQ4,1.0]])],"derivedFrom":subQ3}),-1.0]])]});}
            var Q10;
            {var subQ0=sQuery(id+"F4.wireOp",EDGE,"E80.8");var subQ1=sQuery(id+"F4.wireOp",EDGE,"E79.16");var subQ2=makeQuery(id+"F4.imprint","INTERSECT",VERTEX,{"derivedFrom":[subQ1,subQ0]});Q10=makeQuery(id+"F4.imprint","IMPRINT",FACE,{"disambiguationData":[TD([[makeQuery(id+"F4.imprint","IMPRINT",EDGE,{"disambiguationData":[TD([[subQ2,-1.0]])],"derivedFrom":subQ1}),-1.0]])]});}
            var Q11;
            {var subQ0=sQuery(id+"F4.wireOp",EDGE,"E80.8");var subQ1=sQuery(id+"F4.wireOp",EDGE,"E79.18");var subQ2=makeQuery(id+"F4.imprint","INTERSECT",VERTEX,{"derivedFrom":[subQ1,subQ0]});Q11=makeQuery(id+"F4.imprint","IMPRINT",FACE,{"disambiguationData":[TD([[makeQuery(id+"F4.imprint","IMPRINT",EDGE,{"disambiguationData":[TD([[subQ2,1.0]])],"derivedFrom":subQ1}),-1.0]])]});}
            extrude(context, id + "F7", {"entities" : qUnion([Q0, Q1, Q2, Q3, Q4, Q5, Q6, Q7, Q8, Q9, Q10, Q11]), "operationType" : NewBodyOperationType.ADD, "depth" : .5 * mm});
        }
        {
            var Q0;
            Q0=makeQuery(id+"F7.opExtrude","CAP_EDGE",EDGE,{"disambiguationData":[OSD([sQuery(id+"F4.wireOp",EDGE,"E79.47")])],"isStart":false});
            var Q1;
            Q1=makeQuery(id+"F7.opExtrude","CAP_EDGE",EDGE,{"disambiguationData":[OSD([sQuery(id+"F4.wireOp",EDGE,"E79.48")])],"isStart":false});
            var Q2;
            Q2=makeQuery(id+"F7.opExtrude","CAP_EDGE",EDGE,{"disambiguationData":[OSD([sQuery(id+"F4.wireOp",EDGE,"E79.62")])],"isStart":false});
            var Q3;
            Q3=makeQuery(id+"F7.opExtrude","CAP_EDGE",EDGE,{"disambiguationData":[OSD([sQuery(id+"F4.wireOp",EDGE,"E79.4")])],"isStart":false});
            var Q4;
            Q4=makeQuery(id+"F7.opExtrude","CAP_EDGE",EDGE,{"disambiguationData":[OSD([sQuery(id+"F4.wireOp",EDGE,"E79.3")])],"isStart":false});
            var Q5;
            Q5=makeQuery(id+"F7.opExtrude","CAP_EDGE",EDGE,{"disambiguationData":[OSD([sQuery(id+"F4.wireOp",EDGE,"E79.40")])],"isStart":false});
            var Q6;
            Q6=makeQuery(id+"F7.opExtrude","CAP_EDGE",EDGE,{"disambiguationData":[OSD([sQuery(id+"F4.wireOp",EDGE,"E79.9")])],"isStart":false});
            var Q7;
            Q7=makeQuery(id+"F7.opExtrude","CAP_EDGE",EDGE,{"disambiguationData":[OSD([sQuery(id+"F4.wireOp",EDGE,"E79.11")])],"isStart":false});
            var Q8;
            Q8=makeQuery(id+"F7.opExtrude","CAP_EDGE",EDGE,{"disambiguationData":[OSD([sQuery(id+"F4.wireOp",EDGE,"E79.35")])],"isStart":false});
            var Q9;
            Q9=makeQuery(id+"F7.opExtrude","CAP_EDGE",EDGE,{"disambiguationData":[OSD([sQuery(id+"F4.wireOp",EDGE,"E79.33")])],"isStart":false});
            var Q10;
            Q10=makeQuery(id+"F7.opExtrude","CAP_EDGE",EDGE,{"disambiguationData":[OSD([sQuery(id+"F4.wireOp",EDGE,"E79.16")])],"isStart":false});
            var Q11;
            Q11=makeQuery(id+"F7.opExtrude","CAP_EDGE",EDGE,{"disambiguationData":[OSD([sQuery(id+"F4.wireOp",EDGE,"E79.18")])],"isStart":false});
            var Q12;
            Q12=makeQuery(id+"F7.opExtrude","CAP_EDGE",EDGE,{"disambiguationData":[OSD([sQuery(id+"F4.wireOp",EDGE,"E79.10")])],"isStart":false});
            var Q13;
            Q13=makeQuery(id+"F2.opExtrude","CAP_EDGE",EDGE,{"disambiguationData":[OSD([sQuery(id+"F1.wireOp",EDGE,"E69")])],"isStart":false});
            var Q14;
            Q14=makeQuery(id+"F3.opExtrude","CAP_EDGE",EDGE,{"disambiguationData":[OSD([sQuery(id+"F1.wireOp",EDGE,"E69")])],"isStart":false});
            fillet(context, id + "F8", {"entities" : qUnion([Q0, Q1, Q2, Q3, Q4, Q5, Q6, Q7, Q8, Q9, Q10, Q11, Q12, Q13, Q14]), "radius" : .5 * mm, "tangentPropagation" : true, "allowEdgeOverflow" : false});
        }
    });
